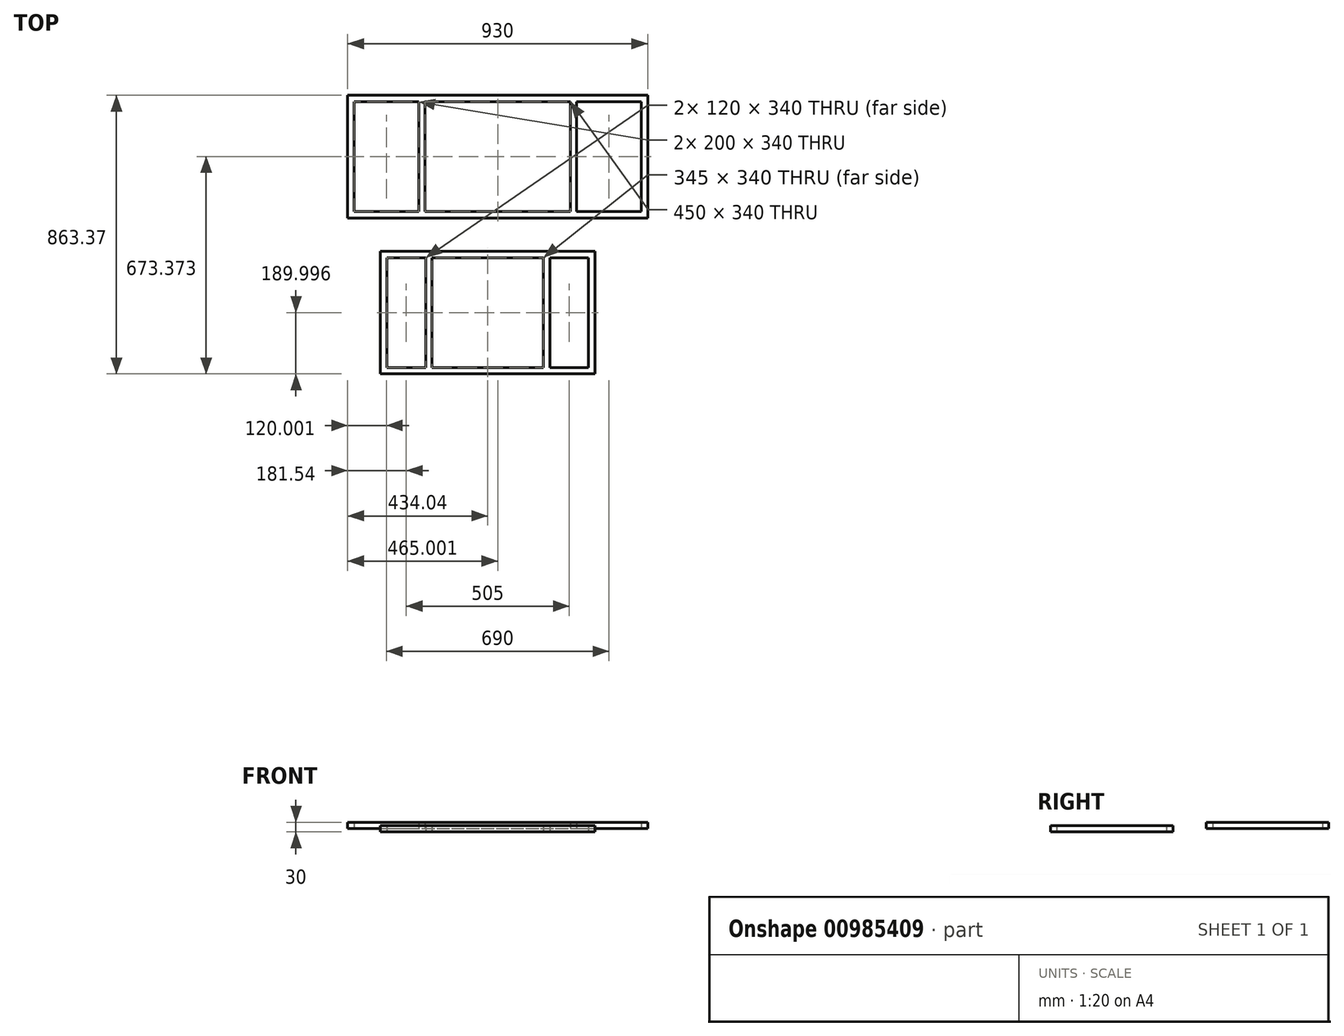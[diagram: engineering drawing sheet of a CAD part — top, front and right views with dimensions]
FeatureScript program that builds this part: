
annotation { "Feature Type Name" : "Feature", "Feature Type Description" : "" }
export const myFeature = defineFeature(function(context is Context, id is Id, definition is map)
    precondition{}
    {
        {
            var Q0;
            Q0=qCreatedBy(makeId("Top.planeOp"),FACE);
            var sketch = newSketch(context, id + "F0", { "sketchPlane" : qUnion([Q0])});
            skLineSegment(sketch, "E0.bottom", {"start": v(-160, 257.02) * mm, "end": v(505, 257.02) * mm});
            skLineSegment(sketch, "E0.top", {"start": v(-160, -122.98) * mm, "end": v(505, -122.98) * mm});
            skLineSegment(sketch, "E0.left", {"start": v(-160, 257.02) * mm, "end": v(-160, -122.98) * mm});
            skLineSegment(sketch, "E0.right", {"start": v(505, 257.02) * mm, "end": v(505, -122.98) * mm});
            skLineSegment(sketch, "E1.bottom", {"start": v(-140, 237.02) * mm, "end": v(-20, 237.02) * mm});
            skLineSegment(sketch, "E1.top", {"start": v(-140, -102.98) * mm, "end": v(-20, -102.98) * mm});
            skLineSegment(sketch, "E1.left", {"start": v(-140, 237.02) * mm, "end": v(-140, -102.98) * mm});
            skLineSegment(sketch, "E1.right", {"start": v(-20, 237.02) * mm, "end": v(-20, -102.98) * mm});
            skLineSegment(sketch, "E2.1.0.0", {"start": v(485, 237.02) * mm, "end": v(485, -102.98) * mm});
            skLineSegment(sketch, "E2.1.0.1", {"start": v(365, 237.02) * mm, "end": v(485, 237.02) * mm});
            skLineSegment(sketch, "E2.1.0.2", {"start": v(365, 237.02) * mm, "end": v(365, -102.98) * mm});
            skLineSegment(sketch, "E2.1.0.3", {"start": v(365, -102.98) * mm, "end": v(485, -102.98) * mm});
            skLineSegment(sketch, "E2.direction1", {"start": v(-20, -102.98) * mm, "end": v(485, -102.98) * mm, "construction": true});
            skLineSegment(sketch, "E3.bottom", {"start": v(0, 237.02) * mm, "end": v(345, 237.02) * mm});
            skLineSegment(sketch, "E3.top", {"start": v(0, -102.98) * mm, "end": v(345, -102.98) * mm});
            skLineSegment(sketch, "E3.left", {"start": v(0, 237.02) * mm, "end": v(0, -102.98) * mm});
            skLineSegment(sketch, "E3.right", {"start": v(345, 237.02) * mm, "end": v(345, -102.98) * mm});
            skSolve(sketch);
        }
        {
            var Q0;
            Q0=qCreatedBy(makeId("Top.planeOp"),FACE);
            var sketch = newSketch(context, id + "F1", { "sketchPlane" : qUnion([Q0])});
            skLineSegment(sketch, "E4.bottom", {"start": v(-261.54, 740.4) * mm, "end": v(668.46, 740.4) * mm});
            skLineSegment(sketch, "E4.top", {"start": v(-261.54, 360.4) * mm, "end": v(668.46, 360.4) * mm});
            skLineSegment(sketch, "E4.left", {"start": v(-261.54, 740.4) * mm, "end": v(-261.54, 360.4) * mm});
            skLineSegment(sketch, "E4.right", {"start": v(668.46, 740.4) * mm, "end": v(668.46, 360.4) * mm});
            skLineSegment(sketch, "E5.bottom", {"start": v(-241.54, 720.4) * mm, "end": v(-41.54, 720.4) * mm});
            skLineSegment(sketch, "E5.top", {"start": v(-241.54, 380.4) * mm, "end": v(-41.54, 380.4) * mm});
            skLineSegment(sketch, "E5.left", {"start": v(-241.54, 720.4) * mm, "end": v(-241.54, 380.4) * mm});
            skLineSegment(sketch, "E5.right", {"start": v(-41.54, 720.4) * mm, "end": v(-41.54, 380.4) * mm});
            skLineSegment(sketch, "E6.1.0.0", {"start": v(648.46, 720.4) * mm, "end": v(648.46, 380.4) * mm});
            skLineSegment(sketch, "E6.1.0.1", {"start": v(448.46, 720.4) * mm, "end": v(648.46, 720.4) * mm});
            skLineSegment(sketch, "E6.1.0.2", {"start": v(448.46, 720.4) * mm, "end": v(448.46, 380.4) * mm});
            skLineSegment(sketch, "E6.1.0.3", {"start": v(448.46, 380.4) * mm, "end": v(648.46, 380.4) * mm});
            skLineSegment(sketch, "E6.direction1", {"start": v(-41.54, 380.4) * mm, "end": v(648.46, 380.4) * mm, "construction": true});
            skLineSegment(sketch, "E7.bottom", {"start": v(-21.54, 720.4) * mm, "end": v(428.46, 720.4) * mm});
            skLineSegment(sketch, "E7.top", {"start": v(-21.54, 380.4) * mm, "end": v(428.46, 380.4) * mm});
            skLineSegment(sketch, "E7.left", {"start": v(-21.54, 720.4) * mm, "end": v(-21.54, 380.4) * mm});
            skLineSegment(sketch, "E7.right", {"start": v(428.46, 720.4) * mm, "end": v(428.46, 380.4) * mm});
            skSolve(sketch);
        }
        {
            var Q0;
            Q0=makeQuery(id+"F0.imprint","IMPRINT",FACE,{"disambiguationData":[TD([[makeQuery(id+"F0.imprint","IMPRINT",EDGE,{"derivedFrom":sQuery(id+"F0.wireOp",EDGE,"E0.bottom")}),-1.0]])]});
            extrude(context, id + "F2", {"entities" : qUnion([Q0]), "endBound" : BoundingType.SYMMETRIC, "depth" : 20 * mm, "offsetDistance" : 25 * mm});
        }
        {
            var Q0;
            Q0=makeQuery(id+"F1.imprint","IMPRINT",FACE,{"disambiguationData":[TD([[makeQuery(id+"F1.imprint","IMPRINT",EDGE,{"derivedFrom":sQuery(id+"F1.wireOp",EDGE,"E4.bottom")}),-1.0]])]});
            extrude(context, id + "F3", {"entities" : qUnion([Q0]), "depth" : 20 * mm, "offsetDistance" : 25 * mm});
        }
    });
